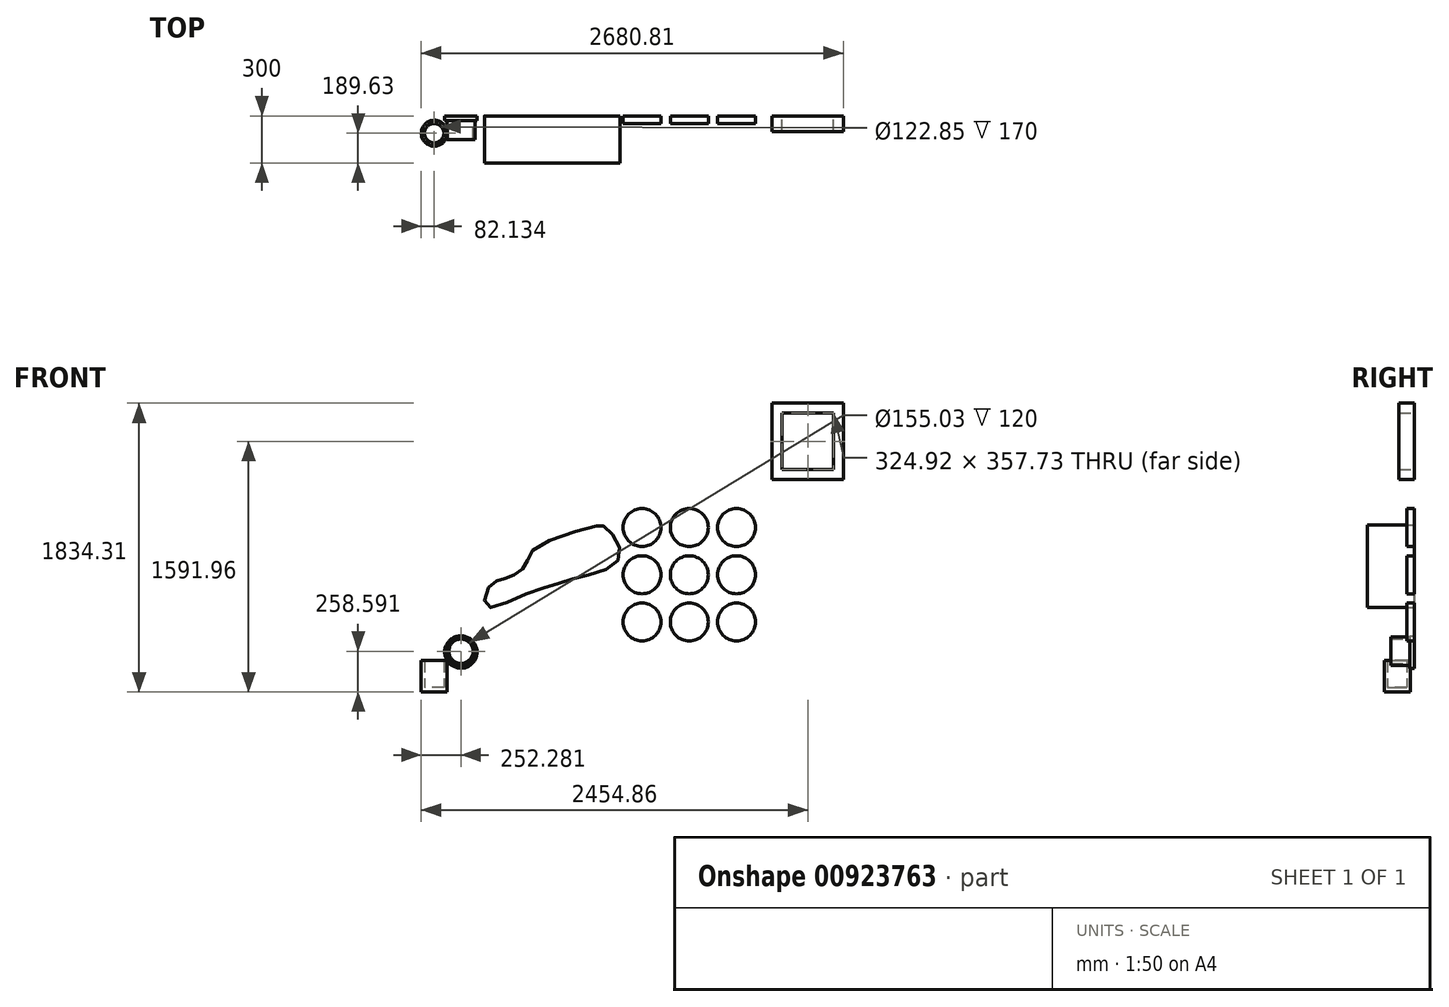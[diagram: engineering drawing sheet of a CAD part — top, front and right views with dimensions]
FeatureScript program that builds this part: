
annotation { "Feature Type Name" : "Feature", "Feature Type Description" : "" }
export const myFeature = defineFeature(function(context is Context, id is Id, definition is map)
    precondition{}
    {
        {
            var Q0;
            Q0=qCreatedBy(makeId("Top.planeOp"),FACE);
            var sketch = newSketch(context, id + "F0", { "sketchPlane" : qUnion([Q0])});
            skCircle(sketch, "E0", {"center": v(-287.74, -110.37) * mm, "radius": 82.13 * mm});
            skCircle(sketch, "E1", {"center": v(-287.74, -110.37) * mm, "radius": 61.43 * mm});
            skSolve(sketch);
        }
        {
            var Q0;
            Q0 = qSketchRegion(id + "F0", true);
            extrude(context, id + "F1", {"entities" : qUnion([Q0]), "depth" : 200 * mm, "offsetDistance" : 25 * mm});
        }
        {
            var Q0;
            Q0=qCreatedBy(makeId("Top.planeOp"),FACE);
            var sketch = newSketch(context, id + "F2", { "sketchPlane" : qUnion([Q0])});
            skCircle(sketch, "E2", {"center": v(-288.88, -110.32) * mm, "radius": 71.54 * mm});
            skSolve(sketch);
        }
        {
            var Q0;
            Q0 = qSketchRegion(id + "F2", true);
            extrude(context, id + "F3", {"entities" : qUnion([Q0]), "operationType" : NewBodyOperationType.ADD, "depth" : 30 * mm, "offsetDistance" : 25 * mm});
        }
        {
            var Q0;
            Q0=qCreatedBy(makeId("Front.planeOp"),FACE);
            var sketch = newSketch(context, id + "F4", { "sketchPlane" : qUnion([Q0])});
            skCircle(sketch, "E3", {"center": v(-117.59, 258.6) * mm, "radius": 89.52 * mm});
            skCircle(sketch, "E4", {"center": v(-117.59, 258.6) * mm, "radius": 77.52 * mm});
            skSolve(sketch);
        }
        {
            var Q0;
            Q0 = qSketchRegion(id + "F4", true);
            extrude(context, id + "F5", {"entities" : qUnion([Q0]), "depth" : 150 * mm, "offsetDistance" : 25 * mm});
        }
        {
            var Q0;
            Q0=qCreatedBy(makeId("Front.planeOp"),FACE);
            var sketch = newSketch(context, id + "F6", { "sketchPlane" : qUnion([Q0])});
            skCircle(sketch, "E5", {"center": v(-118.3, 253.44) * mm, "radius": 102.6 * mm});
            skSolve(sketch);
        }
        {
            var Q0;
            Q0 = qSketchRegion(id + "F6", true);
            extrude(context, id + "F7", {"entities" : qUnion([Q0]), "operationType" : NewBodyOperationType.ADD, "depth" : 30 * mm, "offsetDistance" : 25 * mm});
        }
        {
            var Q0;
            Q0=qCreatedBy(makeId("Front.planeOp"),FACE);
            var sketch = newSketch(context, id + "F8", { "sketchPlane" : qUnion([Q0])});
            skFitSpline(sketch, "E6", {"points": [v(57.35, 665.34) * mm, v(121.52, 709.26) * mm, v(181.25, 728.62) * mm, v(251.72, 761.66) * mm, v(303.28, 829.44) * mm, v(359.23, 917.53) * mm, v(760.38, 1058.73) * mm, v(785.9, 1055.52) * mm, v(874.66, 960.53) * mm, v(871.6, 826.34) * mm, v(664.52, 736.94) * mm, v(487.49, 685.83) * mm, v(252.77, 603.26) * mm, v(41.62, 544.43) * mm, v(57.35, 665.34) * mm]});
            skSolve(sketch);
        }
        {
            var Q0;
            Q0 = qSketchRegion(id + "F8", true);
            extrude(context, id + "F9", {"entities" : qUnion([Q0]), "depth" : 300 * mm, "offsetDistance" : 25 * mm});
        }
        {
            var Q0;
            Q0=qCreatedBy(makeId("Front.planeOp"),FACE);
            var sketch = newSketch(context, id + "F10", { "sketchPlane" : qUnion([Q0])});
            skCircle(sketch, "E7", {"center": v(1032.56, 444.29) * mm, "radius": 120.56 * mm});
            skCircle(sketch, "E8.0.1.0", {"center": v(1032.56, 744.29) * mm, "radius": 120.56 * mm});
            skCircle(sketch, "E8.0.2.0", {"center": v(1032.56, 1044.29) * mm, "radius": 120.56 * mm});
            skCircle(sketch, "E8.1.0.0", {"center": v(1332.56, 444.29) * mm, "radius": 120.56 * mm});
            skCircle(sketch, "E8.1.1.0", {"center": v(1332.56, 744.29) * mm, "radius": 120.56 * mm});
            skCircle(sketch, "E8.1.2.0", {"center": v(1332.56, 1044.29) * mm, "radius": 120.56 * mm});
            skCircle(sketch, "E8.2.0.0", {"center": v(1632.56, 444.29) * mm, "radius": 120.56 * mm});
            skCircle(sketch, "E8.2.1.0", {"center": v(1632.56, 744.29) * mm, "radius": 120.56 * mm});
            skCircle(sketch, "E8.2.2.0", {"center": v(1632.56, 1044.29) * mm, "radius": 120.56 * mm});
            skLineSegment(sketch, "E8.direction1", {"start": v(1032.56, 444.29) * mm, "end": v(1332.56, 444.29) * mm, "construction": true});
            skLineSegment(sketch, "E8.direction2", {"start": v(1032.56, 444.29) * mm, "end": v(1032.56, 744.29) * mm, "construction": true});
            skSolve(sketch);
        }
        {
            var Q0;
            Q0 = qSketchRegion(id + "F10", true);
            extrude(context, id + "F11", {"entities" : qUnion([Q0]), "depth" : 50 * mm, "offsetDistance" : 25 * mm});
        }
        {
            var Q0;
            Q0=qCreatedBy(makeId("Front.planeOp"),FACE);
            var sketch = newSketch(context, id + "F12", { "sketchPlane" : qUnion([Q0])});
            skLineSegment(sketch, "E9.bottom", {"start": v(1922.53, 1770.82) * mm, "end": v(2247.46, 1770.82) * mm});
            skLineSegment(sketch, "E9.top", {"start": v(1922.53, 1413.1) * mm, "end": v(2247.46, 1413.1) * mm});
            skLineSegment(sketch, "E9.left", {"start": v(1922.53, 1770.82) * mm, "end": v(1922.53, 1413.1) * mm});
            skLineSegment(sketch, "E9.right", {"start": v(2247.46, 1770.82) * mm, "end": v(2247.46, 1413.1) * mm});
            skLineSegment(sketch, "E10.0", {"start": v(1859.05, 1834.3) * mm, "end": v(2310.94, 1834.3) * mm});
            skLineSegment(sketch, "E10.1", {"start": v(1859.05, 1834.3) * mm, "end": v(1859.05, 1349.6) * mm});
            skLineSegment(sketch, "E10.2", {"start": v(1859.05, 1349.6) * mm, "end": v(2310.94, 1349.6) * mm});
            skLineSegment(sketch, "E10.3", {"start": v(2310.94, 1834.3) * mm, "end": v(2310.94, 1349.6) * mm});
            skSolve(sketch);
        }
        {
            var Q0;
            Q0 = qSketchRegion(id + "F12", true);
            extrude(context, id + "F13", {"entities" : qUnion([Q0]), "depth" : 100 * mm, "offsetDistance" : 25 * mm});
        }
    });
